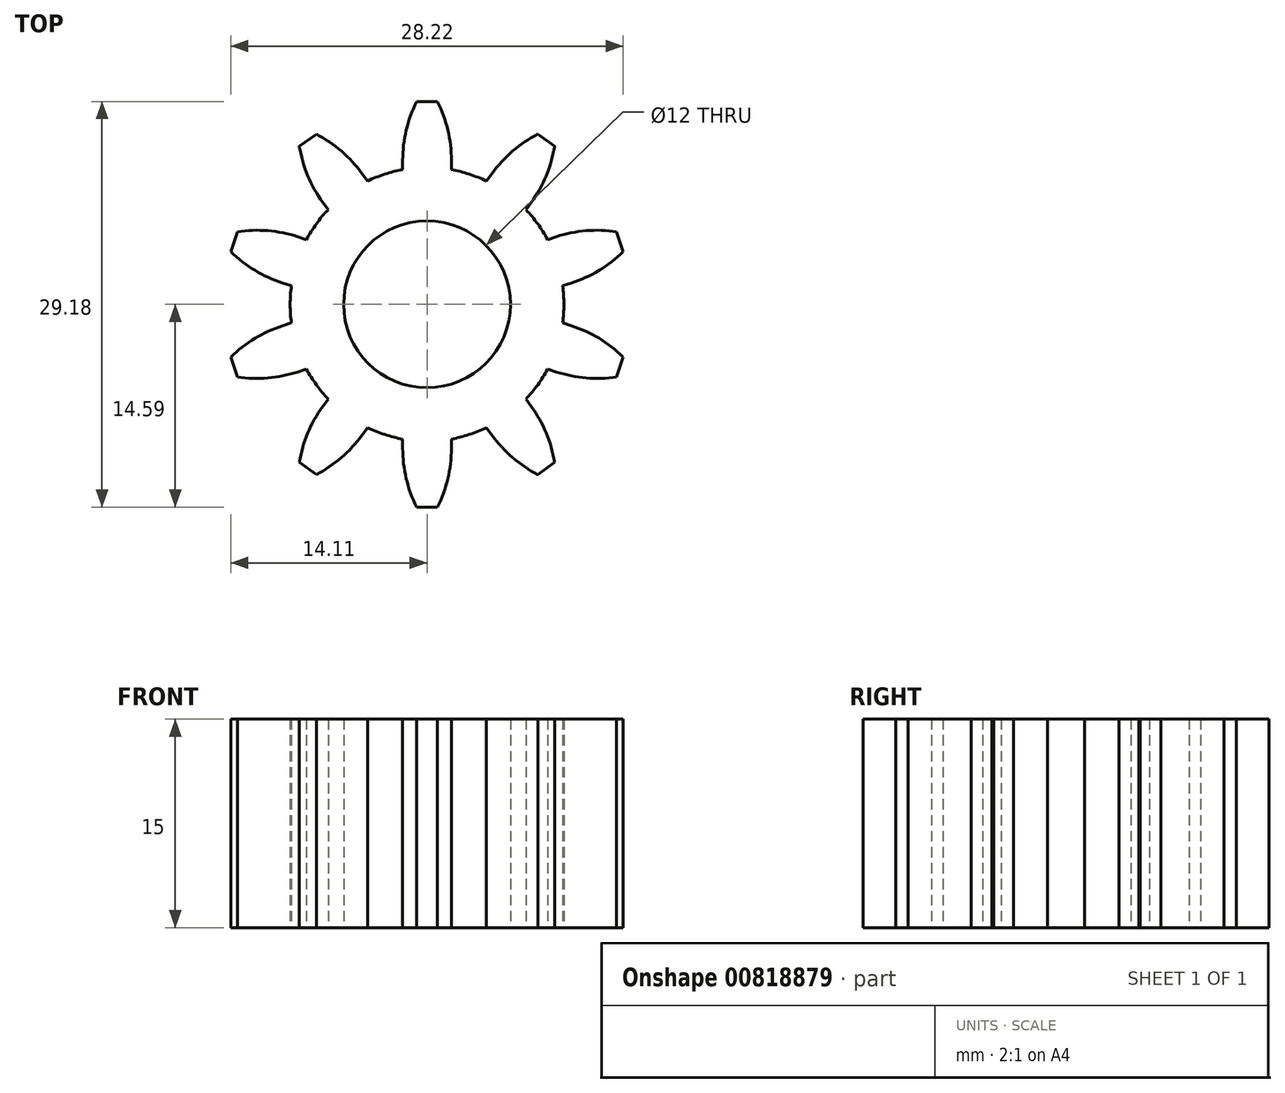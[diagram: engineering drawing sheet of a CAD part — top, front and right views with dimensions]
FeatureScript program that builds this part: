
annotation { "Feature Type Name" : "Feature", "Feature Type Description" : "" }
export const myFeature = defineFeature(function(context is Context, id is Id, definition is map)
    precondition{}
    {
        {
            var Q0;
            Q0=qCreatedBy(makeId("Top.planeOp"),FACE);
            var sketch = newSketch(context, id + "F0", { "sketchPlane" : qUnion([Q0])});
            skCircle(sketch, "E0", {"center": v(0, 0) * mm, "radius": 6 * mm});
            skCircle(sketch, "E1", {"center": v(0, 0) * mm, "radius": 9.85 * mm});
            skLineSegment(sketch, "E2", {"start": v(-1.75, 9.7) * mm, "end": v(-1.75, 12.6) * mm});
            skLineSegment(sketch, "E3", {"start": v(-1.75, 12.6) * mm, "end": v(-0.75, 14.6) * mm});
            skLineSegment(sketch, "E4", {"start": v(-0.75, 14.6) * mm, "end": v(0.75, 14.6) * mm});
            skLineSegment(sketch, "E5", {"start": v(0.75, 14.6) * mm, "end": v(1.75, 12.6) * mm});
            skLineSegment(sketch, "E6", {"start": v(1.75, 12.6) * mm, "end": v(1.75, 9.7) * mm});
            skLineSegment(sketch, "E7.1.0", {"start": v(-7.97, 12.25) * mm, "end": v(-5.99, 11.22) * mm});
            skLineSegment(sketch, "E7.1.1", {"start": v(-9.18, 11.37) * mm, "end": v(-7.97, 12.25) * mm});
            skLineSegment(sketch, "E7.1.2", {"start": v(-8.82, 9.16) * mm, "end": v(-9.18, 11.37) * mm});
            skLineSegment(sketch, "E7.1.3", {"start": v(-7.11, 6.81) * mm, "end": v(-8.82, 9.16) * mm});
            skLineSegment(sketch, "E7.1.4", {"start": v(-5.99, 11.22) * mm, "end": v(-4.28, 8.87) * mm});
            skLineSegment(sketch, "E7.2.0", {"start": v(-13.65, 5.22) * mm, "end": v(-11.44, 5.56) * mm});
            skLineSegment(sketch, "E7.2.1", {"start": v(-14.11, 3.8) * mm, "end": v(-13.65, 5.22) * mm});
            skLineSegment(sketch, "E7.2.2", {"start": v(-12.52, 2.23) * mm, "end": v(-14.11, 3.8) * mm});
            skLineSegment(sketch, "E7.2.3", {"start": v(-9.76, 1.33) * mm, "end": v(-12.52, 2.23) * mm});
            skLineSegment(sketch, "E7.2.4", {"start": v(-11.44, 5.56) * mm, "end": v(-8.68, 4.66) * mm});
            skLineSegment(sketch, "E7.3.0", {"start": v(-14.11, -3.8) * mm, "end": v(-12.52, -2.23) * mm});
            skLineSegment(sketch, "E7.3.1", {"start": v(-13.65, -5.22) * mm, "end": v(-14.11, -3.8) * mm});
            skLineSegment(sketch, "E7.3.2", {"start": v(-11.44, -5.56) * mm, "end": v(-13.65, -5.22) * mm});
            skLineSegment(sketch, "E7.3.3", {"start": v(-8.68, -4.66) * mm, "end": v(-11.44, -5.56) * mm});
            skLineSegment(sketch, "E7.3.4", {"start": v(-12.52, -2.23) * mm, "end": v(-9.76, -1.33) * mm});
            skLineSegment(sketch, "E7.4.0", {"start": v(-9.18, -11.37) * mm, "end": v(-8.82, -9.16) * mm});
            skLineSegment(sketch, "E7.4.1", {"start": v(-7.97, -12.25) * mm, "end": v(-9.18, -11.37) * mm});
            skLineSegment(sketch, "E7.4.2", {"start": v(-5.99, -11.22) * mm, "end": v(-7.97, -12.25) * mm});
            skLineSegment(sketch, "E7.4.3", {"start": v(-4.28, -8.87) * mm, "end": v(-5.99, -11.22) * mm});
            skLineSegment(sketch, "E7.4.4", {"start": v(-8.82, -9.16) * mm, "end": v(-7.11, -6.81) * mm});
            skLineSegment(sketch, "E7.5.0", {"start": v(-0.75, -14.6) * mm, "end": v(-1.75, -12.6) * mm});
            skLineSegment(sketch, "E7.5.1", {"start": v(0.75, -14.6) * mm, "end": v(-0.75, -14.6) * mm});
            skLineSegment(sketch, "E7.5.2", {"start": v(1.75, -12.6) * mm, "end": v(0.75, -14.6) * mm});
            skLineSegment(sketch, "E7.5.3", {"start": v(1.75, -9.7) * mm, "end": v(1.75, -12.6) * mm});
            skLineSegment(sketch, "E7.5.4", {"start": v(-1.75, -12.6) * mm, "end": v(-1.75, -9.7) * mm});
            skLineSegment(sketch, "E7.6.0", {"start": v(7.97, -12.25) * mm, "end": v(5.99, -11.22) * mm});
            skLineSegment(sketch, "E7.6.1", {"start": v(9.18, -11.37) * mm, "end": v(7.97, -12.25) * mm});
            skLineSegment(sketch, "E7.6.2", {"start": v(8.82, -9.16) * mm, "end": v(9.18, -11.37) * mm});
            skLineSegment(sketch, "E7.6.3", {"start": v(7.11, -6.81) * mm, "end": v(8.82, -9.16) * mm});
            skLineSegment(sketch, "E7.6.4", {"start": v(5.99, -11.22) * mm, "end": v(4.28, -8.87) * mm});
            skLineSegment(sketch, "E7.7.0", {"start": v(13.65, -5.22) * mm, "end": v(11.44, -5.56) * mm});
            skLineSegment(sketch, "E7.7.1", {"start": v(14.11, -3.8) * mm, "end": v(13.65, -5.22) * mm});
            skLineSegment(sketch, "E7.7.2", {"start": v(12.52, -2.23) * mm, "end": v(14.11, -3.8) * mm});
            skLineSegment(sketch, "E7.7.3", {"start": v(9.76, -1.33) * mm, "end": v(12.52, -2.23) * mm});
            skLineSegment(sketch, "E7.7.4", {"start": v(11.44, -5.56) * mm, "end": v(8.68, -4.66) * mm});
            skLineSegment(sketch, "E7.8.0", {"start": v(14.11, 3.8) * mm, "end": v(12.52, 2.23) * mm});
            skLineSegment(sketch, "E7.8.1", {"start": v(13.65, 5.22) * mm, "end": v(14.11, 3.8) * mm});
            skLineSegment(sketch, "E7.8.2", {"start": v(11.44, 5.56) * mm, "end": v(13.65, 5.22) * mm});
            skLineSegment(sketch, "E7.8.3", {"start": v(8.68, 4.66) * mm, "end": v(11.44, 5.56) * mm});
            skLineSegment(sketch, "E7.8.4", {"start": v(12.52, 2.23) * mm, "end": v(9.76, 1.33) * mm});
            skLineSegment(sketch, "E7.9.0", {"start": v(9.18, 11.37) * mm, "end": v(8.82, 9.16) * mm});
            skLineSegment(sketch, "E7.9.1", {"start": v(7.97, 12.25) * mm, "end": v(9.18, 11.37) * mm});
            skLineSegment(sketch, "E7.9.2", {"start": v(5.99, 11.22) * mm, "end": v(7.97, 12.25) * mm});
            skLineSegment(sketch, "E7.9.3", {"start": v(4.28, 8.87) * mm, "end": v(5.99, 11.22) * mm});
            skLineSegment(sketch, "E7.9.4", {"start": v(8.82, 9.16) * mm, "end": v(7.11, 6.81) * mm});
            skCircle(sketch, "E8", {"center": v(0, 0) * mm, "radius": 14.61 * mm});
            skSolve(sketch);
        }
        {
            var Q0;
            Q0=makeQuery(id+"F0.imprint","IMPRINT",FACE,{"disambiguationData":[TD([[makeQuery(id+"F0.imprint","IMPRINT",EDGE,{"derivedFrom":sQuery(id+"F0.wireOp",EDGE,"E7.7.0")}),-1.0]])]});
            var Q1;
            Q1=makeQuery(id+"F0.imprint","IMPRINT",FACE,{"disambiguationData":[TD([[makeQuery(id+"F0.imprint","IMPRINT",EDGE,{"derivedFrom":sQuery(id+"F0.wireOp",EDGE,"E7.6.0")}),-1.0]])]});
            var Q2;
            Q2=makeQuery(id+"F0.imprint","IMPRINT",FACE,{"disambiguationData":[TD([[makeQuery(id+"F0.imprint","IMPRINT",EDGE,{"derivedFrom":sQuery(id+"F0.wireOp",EDGE,"E0")}),-1.0]])]});
            var Q3;
            Q3=makeQuery(id+"F0.imprint","IMPRINT",FACE,{"disambiguationData":[TD([[makeQuery(id+"F0.imprint","IMPRINT",EDGE,{"derivedFrom":sQuery(id+"F0.wireOp",EDGE,"E7.8.0")}),-1.0]])]});
            var Q4;
            Q4=makeQuery(id+"F0.imprint","IMPRINT",FACE,{"disambiguationData":[TD([[makeQuery(id+"F0.imprint","IMPRINT",EDGE,{"derivedFrom":sQuery(id+"F0.wireOp",EDGE,"E7.9.0")}),-1.0]])]});
            var Q5;
            {var subQ0=sQuery(id+"F0.wireOp",EDGE,"E2");Q5=makeQuery(id+"F0.imprint","IMPRINT",FACE,{"disambiguationData":[TD([[makeQuery(id+"F0.imprint","IMPRINT",EDGE,{"derivedFrom":subQ0}),-1.0]])]});}
            var Q6;
            Q6=makeQuery(id+"F0.imprint","IMPRINT",FACE,{"disambiguationData":[TD([[makeQuery(id+"F0.imprint","IMPRINT",EDGE,{"derivedFrom":sQuery(id+"F0.wireOp",EDGE,"E7.1.0")}),-1.0]])]});
            var Q7;
            Q7=makeQuery(id+"F0.imprint","IMPRINT",FACE,{"disambiguationData":[TD([[makeQuery(id+"F0.imprint","IMPRINT",EDGE,{"derivedFrom":sQuery(id+"F0.wireOp",EDGE,"E7.2.0")}),-1.0]])]});
            var Q8;
            Q8=makeQuery(id+"F0.imprint","IMPRINT",FACE,{"disambiguationData":[TD([[makeQuery(id+"F0.imprint","IMPRINT",EDGE,{"derivedFrom":sQuery(id+"F0.wireOp",EDGE,"E7.3.0")}),-1.0]])]});
            var Q9;
            Q9=makeQuery(id+"F0.imprint","IMPRINT",FACE,{"disambiguationData":[TD([[makeQuery(id+"F0.imprint","IMPRINT",EDGE,{"derivedFrom":sQuery(id+"F0.wireOp",EDGE,"E7.4.0")}),-1.0]])]});
            var Q10;
            Q10=makeQuery(id+"F0.imprint","IMPRINT",FACE,{"disambiguationData":[TD([[makeQuery(id+"F0.imprint","IMPRINT",EDGE,{"derivedFrom":sQuery(id+"F0.wireOp",EDGE,"E7.5.0")}),-1.0]])]});
            extrude(context, id + "F1", {"entities" : qUnion([Q0, Q1, Q2, Q3, Q4, Q5, Q6, Q7, Q8, Q9, Q10]), "depth" : 15 * mm, "offsetDistance" : 25 * mm});
        }
        {
            var Q0;
            Q0=makeQuery(id+"F1.opExtrude","SWEPT_EDGE",EDGE,{"disambiguationData":[OSD([sQuery(id+"F0.wireOp",EDGE,"E7.6.2"),sQuery(id+"F0.wireOp",EDGE,"E7.6.3")])]});
            var Q1;
            Q1=makeQuery(id+"F1.opExtrude","SWEPT_EDGE",EDGE,{"disambiguationData":[OSD([sQuery(id+"F0.wireOp",EDGE,"E7.6.0"),sQuery(id+"F0.wireOp",EDGE,"E7.6.4")])]});
            var Q2;
            Q2=makeQuery(id+"F1.opExtrude","SWEPT_EDGE",EDGE,{"disambiguationData":[OSD([sQuery(id+"F0.wireOp",EDGE,"E7.7.0"),sQuery(id+"F0.wireOp",EDGE,"E7.7.4")])]});
            var Q3;
            Q3=makeQuery(id+"F1.opExtrude","SWEPT_EDGE",EDGE,{"disambiguationData":[OSD([sQuery(id+"F0.wireOp",EDGE,"E7.7.2"),sQuery(id+"F0.wireOp",EDGE,"E7.7.3")])]});
            var Q4;
            Q4=makeQuery(id+"F1.opExtrude","SWEPT_EDGE",EDGE,{"disambiguationData":[OSD([sQuery(id+"F0.wireOp",EDGE,"E7.8.0"),sQuery(id+"F0.wireOp",EDGE,"E7.8.4")])]});
            var Q5;
            Q5=makeQuery(id+"F1.opExtrude","SWEPT_EDGE",EDGE,{"disambiguationData":[OSD([sQuery(id+"F0.wireOp",EDGE,"E7.8.2"),sQuery(id+"F0.wireOp",EDGE,"E7.8.3")])]});
            var Q6;
            Q6=makeQuery(id+"F1.opExtrude","SWEPT_EDGE",EDGE,{"disambiguationData":[OSD([sQuery(id+"F0.wireOp",EDGE,"E7.9.0"),sQuery(id+"F0.wireOp",EDGE,"E7.9.4")])]});
            var Q7;
            Q7=makeQuery(id+"F1.opExtrude","SWEPT_EDGE",EDGE,{"disambiguationData":[OSD([sQuery(id+"F0.wireOp",EDGE,"E7.9.2"),sQuery(id+"F0.wireOp",EDGE,"E7.9.3")])]});
            var Q8;
            Q8=makeQuery(id+"F1.opExtrude","SWEPT_EDGE",EDGE,{"disambiguationData":[OSD([sQuery(id+"F0.wireOp",EDGE,"E5"),sQuery(id+"F0.wireOp",EDGE,"E6")])]});
            var Q9;
            Q9=makeQuery(id+"F1.opExtrude","SWEPT_EDGE",EDGE,{"disambiguationData":[OSD([sQuery(id+"F0.wireOp",EDGE,"E2"),sQuery(id+"F0.wireOp",EDGE,"E3")])]});
            var Q10;
            Q10=makeQuery(id+"F1.opExtrude","SWEPT_EDGE",EDGE,{"disambiguationData":[OSD([sQuery(id+"F0.wireOp",EDGE,"E7.1.0"),sQuery(id+"F0.wireOp",EDGE,"E7.1.4")])]});
            var Q11;
            Q11=makeQuery(id+"F1.opExtrude","SWEPT_EDGE",EDGE,{"disambiguationData":[OSD([sQuery(id+"F0.wireOp",EDGE,"E7.1.2"),sQuery(id+"F0.wireOp",EDGE,"E7.1.3")])]});
            var Q12;
            Q12=makeQuery(id+"F1.opExtrude","SWEPT_EDGE",EDGE,{"disambiguationData":[OSD([sQuery(id+"F0.wireOp",EDGE,"E7.2.0"),sQuery(id+"F0.wireOp",EDGE,"E7.2.4")])]});
            var Q13;
            Q13=makeQuery(id+"F1.opExtrude","SWEPT_EDGE",EDGE,{"disambiguationData":[OSD([sQuery(id+"F0.wireOp",EDGE,"E7.2.2"),sQuery(id+"F0.wireOp",EDGE,"E7.2.3")])]});
            var Q14;
            Q14=makeQuery(id+"F1.opExtrude","SWEPT_EDGE",EDGE,{"disambiguationData":[OSD([sQuery(id+"F0.wireOp",EDGE,"E7.3.0"),sQuery(id+"F0.wireOp",EDGE,"E7.3.4")])]});
            var Q15;
            Q15=makeQuery(id+"F1.opExtrude","SWEPT_EDGE",EDGE,{"disambiguationData":[OSD([sQuery(id+"F0.wireOp",EDGE,"E7.3.2"),sQuery(id+"F0.wireOp",EDGE,"E7.3.3")])]});
            var Q16;
            Q16=makeQuery(id+"F1.opExtrude","SWEPT_EDGE",EDGE,{"disambiguationData":[OSD([sQuery(id+"F0.wireOp",EDGE,"E7.4.0"),sQuery(id+"F0.wireOp",EDGE,"E7.4.4")])]});
            var Q17;
            Q17=makeQuery(id+"F1.opExtrude","SWEPT_EDGE",EDGE,{"disambiguationData":[OSD([sQuery(id+"F0.wireOp",EDGE,"E7.4.2"),sQuery(id+"F0.wireOp",EDGE,"E7.4.3")])]});
            var Q18;
            Q18=makeQuery(id+"F1.opExtrude","SWEPT_EDGE",EDGE,{"disambiguationData":[OSD([sQuery(id+"F0.wireOp",EDGE,"E7.5.0"),sQuery(id+"F0.wireOp",EDGE,"E7.5.4")])]});
            var Q19;
            Q19=makeQuery(id+"F1.opExtrude","SWEPT_EDGE",EDGE,{"disambiguationData":[OSD([sQuery(id+"F0.wireOp",EDGE,"E7.5.2"),sQuery(id+"F0.wireOp",EDGE,"E7.5.3")])]});
            fillet(context, id + "F2", {"entities" : qUnion([Q0, Q1, Q2, Q3, Q4, Q5, Q6, Q7, Q8, Q9, Q10, Q11, Q12, Q13, Q14, Q15, Q16, Q17, Q18, Q19]), "radius" : 9.45 * mm, "tangentPropagation" : true, "allowEdgeOverflow" : false});
        }
    });
